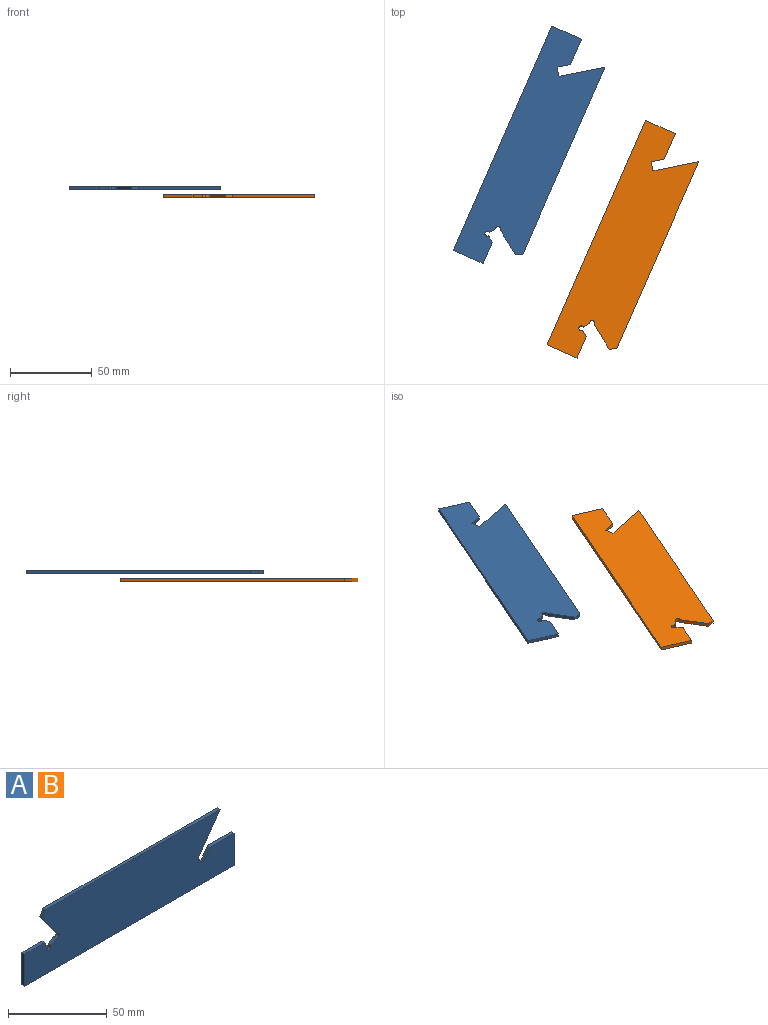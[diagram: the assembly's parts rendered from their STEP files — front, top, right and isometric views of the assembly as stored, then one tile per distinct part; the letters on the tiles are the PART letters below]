
ASSEMBLY  parts=2 mates=1
PART A: 17 faces, bbox 150x2x40 mm
  f0: plane 14.24x2mm, normal (0,0,1), area 28.5mm2, adj f1,f13,f14,f15
  f1: plane 20x2mm, normal (-1,0,0), area 40mm2, adj f0,f2,f14,f15
  f2: plane 150x2mm, normal (0,0,-1), area 300mm2, adj f1,f3,f14,f15
  f3: plane 20x2mm, normal (1,0,0), area 40mm2, adj f2,f4,f14,f15
  f4: plane 16.95x2mm, normal (0,0,1), area 33.9mm2, adj f3,f5,f14,f15
  f5: plane 6.78x4.75mm, normal (-0.82,0,0.57), area 16.6mm2, adj f4,f6,f14,f15
  f6: plane 4.73x3.31mm, normal (0.57,0,0.82), area 11.6mm2, adj f5,f7,f14,f15
  f7: plane 23.47x16.43mm, normal (0.82,0,-0.57), area 57.3mm2, adj f6,f8,f14,f15
  f8: plane 125x2mm, normal (0,0,1), area 250mm2, adj f7,f14,f15,f16
  f9: plane 14.59x10.22mm, normal (-0.82,0,-0.57), area 35.6mm2, adj f10,f14,f15,f16
  f10: cylinder r=1.48mm len=2.96mm, axis (0,1,0), area 11.1mm2, adj f9,f11,f14,f15
  f11: plane 3.7x2.59mm, normal (-0.57,0,0.82), area 9mm2, adj f10,f12,f14,f15
  f12: cylinder r=1.48mm len=2.96mm, axis (0,1,0), area 13.9mm2, adj f11,f13,f14,f15
  f13: plane 3.7x2.59mm, normal (0.82,0,0.57), area 9mm2, adj f0,f12,f14,f15
  f14: plane 150x40mm, normal (0,-1,0), area 5240.1mm2, adj f0,f1,f2,f3,f4,f5,f6,f7
  f15: plane 150x40mm, normal (0,1,0), area 5240.1mm2, adj f0,f1,f2,f3,f4,f5,f6,f7
  f16: plane 4.1x2.13mm, normal (-0.89,0,0.46), area 9.2mm2, adj f8,f9,f14,f15
PART B: same geometry as A
PLACE A rot(axis=(0.73,0.48,0.48),107.4deg) t=(-43.33,-28.31,32.26)mm
PLACE B rot(axis=(0.73,0.48,0.48),107.4deg) t=(14.17,-86.15,27.52)mm
MATE parallel B.f0 <-> A.f0  axis (0.92,-0.4,0) through (35.35,-87.67,26.52)mm
